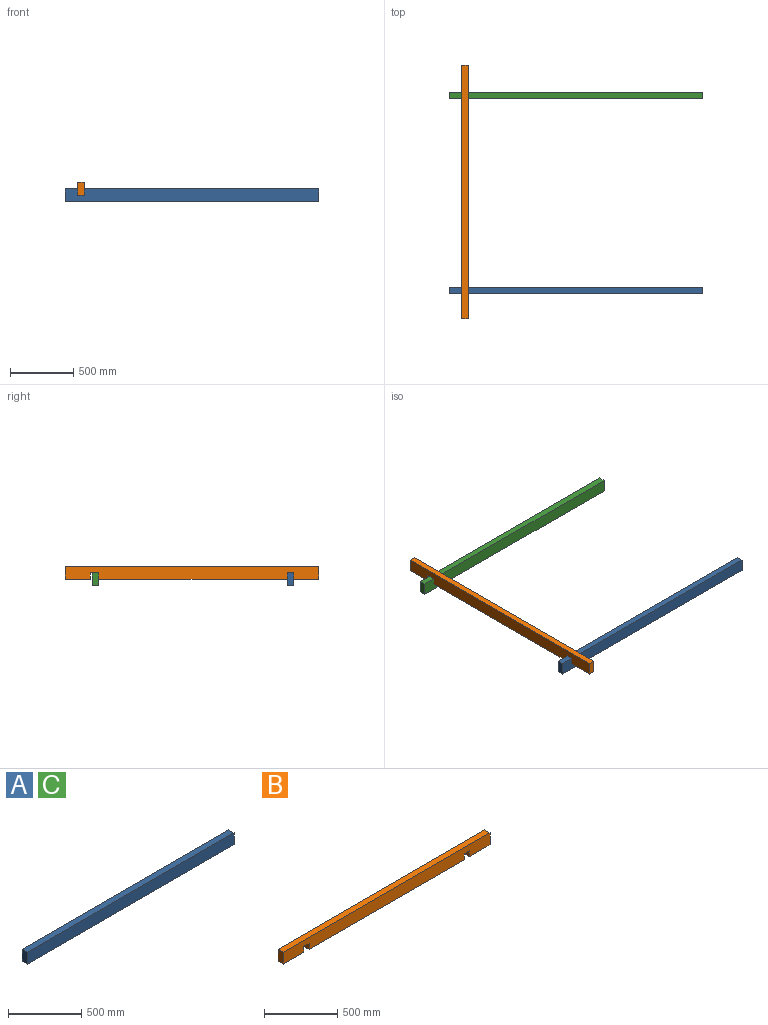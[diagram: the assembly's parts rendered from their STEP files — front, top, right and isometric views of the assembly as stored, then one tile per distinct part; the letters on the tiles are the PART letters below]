
ASSEMBLY  parts=3 mates=2
PART A: 6 faces, bbox 2000x50x100 mm
  f0: plane 2000x50mm, normal (0,0,1), area 100000mm2, adj f1,f3,f4,f5
  f1: plane 2000x100mm, normal (0,-1,0), area 200000mm2, adj f0,f2,f4,f5
  f2: plane 2000x50mm, normal (0,0,-1), area 100000mm2, adj f1,f3,f4,f5
  f3: plane 2000x100mm, normal (0,1,0), area 200000mm2, adj f0,f2,f4,f5
  f4: plane 100x50mm, normal (1,0,0), area 5000mm2, adj f0,f1,f2,f3
  f5: plane 100x50mm, normal (-1,0,0), area 5000mm2, adj f0,f1,f2,f3
PART B: 14 faces, bbox 2000x50x100 mm
  f0: plane 1500x50mm, normal (0,0,-1), area 75000mm2, adj f2,f4,f8,f12
  f1: plane 200x50mm, normal (0,0,-1), area 10000mm2, adj f2,f4,f6,f9
  f2: plane 2000x100mm, normal (0,1,0), area 195000mm2, adj f0,f1,f3,f5,f6,f7,f8,f9
  f3: plane 2000x50mm, normal (0,0,1), area 100000mm2, adj f2,f4,f6,f7
  f4: plane 2000x100mm, normal (0,-1,0), area 195000mm2, adj f0,f1,f3,f5,f6,f7,f8,f9
  f5: plane 200x50mm, normal (0,0,-1), area 10000mm2, adj f2,f4,f7,f11
  f6: plane 100x50mm, normal (1,0,0), area 5000mm2, adj f1,f2,f3,f4
  f7: plane 100x50mm, normal (-1,0,0), area 5000mm2, adj f2,f3,f4,f5
  f8: plane 50x50mm, normal (1,0,0), area 2500mm2, adj f0,f2,f4,f10
  f9: plane 50x50mm, normal (-1,0,0), area 2500mm2, adj f1,f2,f4,f10
  f10: plane 50x50mm, normal (0,0,-1), area 2500mm2, adj f2,f4,f8,f9
  f11: plane 50x50mm, normal (1,0,0), area 2500mm2, adj f2,f4,f5,f13
  f12: plane 50x50mm, normal (-1,0,0), area 2500mm2, adj f0,f2,f4,f13
  f13: plane 50x50mm, normal (0,0,-1), area 2500mm2, adj f2,f4,f11,f12
PART C: same geometry as A
PLACE A at identity fixed
PLACE B rot(axis=(0,0,1),90deg) t=(125,-225,50)mm
PLACE C t=(0,1535.96,0)mm
MATE fastened A.f1 <-> B.f11  axis (0,-1,0) through (0,-25,50)mm
MATE slider C.f1 <-> A.f3  axis (0,-1,0) through (0,1510.96,50)mm
